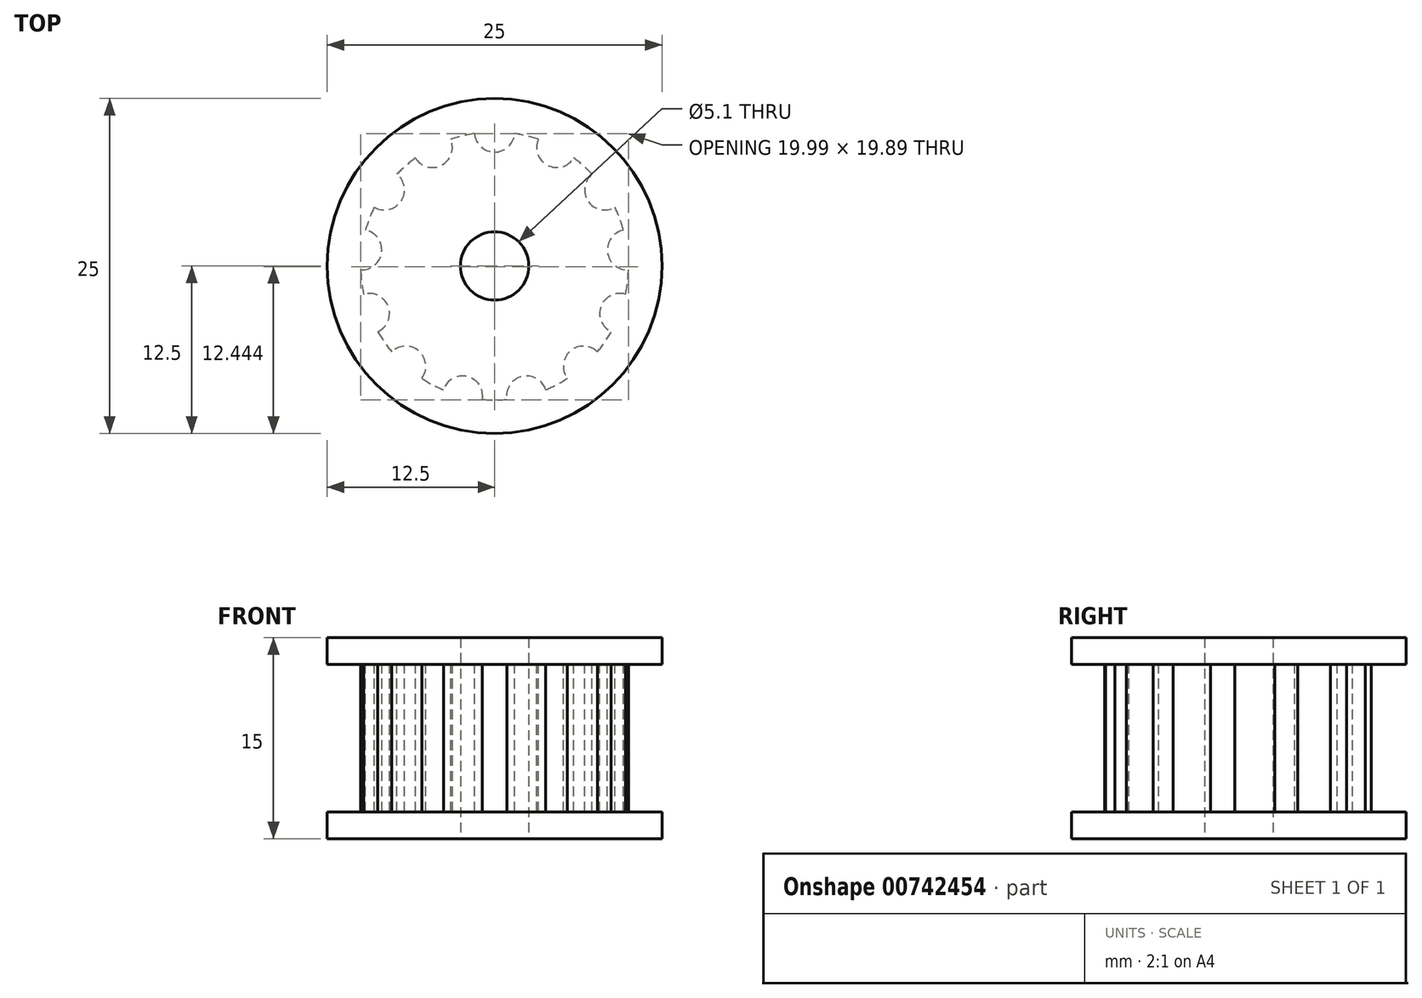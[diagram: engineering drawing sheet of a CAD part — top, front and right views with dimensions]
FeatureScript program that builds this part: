
annotation { "Feature Type Name" : "Feature", "Feature Type Description" : "" }
export const myFeature = defineFeature(function(context is Context, id is Id, definition is map)
    precondition{}
    {
        {
            var Q0;
            Q0=qCreatedBy(makeId("Top.planeOp"),FACE);
            var sketch = newSketch(context, id + "F0", { "sketchPlane" : qUnion([Q0])});
            skCircle(sketch, "E0", {"center": v(0, 0) * mm, "radius": 10 * mm});
            skSolve(sketch);
        }
        {
            var Q0;
            Q0=makeQuery(id+"F0.imprint","IMPRINT",FACE,{"disambiguationData":[TD([[makeQuery(id+"F0.imprint","IMPRINT",EDGE,{"derivedFrom":sQuery(id+"F0.wireOp",EDGE,"E0")}),1.0]])]});
            extrude(context, id + "F1", {"entities" : qUnion([Q0]), "depth" : 11 * mm, "offsetDistance" : 25 * mm});
        }
        {
            var Q0;
            Q0=makeQuery(id+"F1.opExtrude","CAP_FACE",FACE,{"disambiguationData":[OSD([sQuery(id+"F0.wireOp",EDGE,"E0")])],"isStart":false});
            var sketch = newSketch(context, id + "F2", { "sketchPlane" : qUnion([Q0])});
            skLineSegment(sketch, "E1", {"start": v(0, 0) * mm, "end": v(0, 10) * mm, "construction": true});
            skCircle(sketch, "E2", {"center": v(0, 10) * mm, "radius": 1.5 * mm});
            skCircle(sketch, "E3.1.0", {"center": v(-4.65, 8.85) * mm, "radius": 1.5 * mm});
            skCircle(sketch, "E3.2.0", {"center": v(-8.23, 5.68) * mm, "radius": 1.5 * mm});
            skCircle(sketch, "E3.3.0", {"center": v(-9.93, 1.2) * mm, "radius": 1.5 * mm});
            skCircle(sketch, "E3.4.0", {"center": v(-9.35, -3.55) * mm, "radius": 1.5 * mm});
            skCircle(sketch, "E3.5.0", {"center": v(-6.63, -7.49) * mm, "radius": 1.5 * mm});
            skCircle(sketch, "E3.6.0", {"center": v(-2.4, -9.7) * mm, "radius": 1.5 * mm});
            skCircle(sketch, "E3.7.0", {"center": v(2.4, -9.7) * mm, "radius": 1.5 * mm});
            skCircle(sketch, "E3.8.0", {"center": v(6.63, -7.49) * mm, "radius": 1.5 * mm});
            skCircle(sketch, "E3.9.0", {"center": v(9.35, -3.55) * mm, "radius": 1.5 * mm});
            skCircle(sketch, "E3.10.0", {"center": v(9.93, 1.2) * mm, "radius": 1.5 * mm});
            skCircle(sketch, "E3.11.0", {"center": v(8.23, 5.68) * mm, "radius": 1.5 * mm});
            skCircle(sketch, "E3.12.0", {"center": v(4.65, 8.85) * mm, "radius": 1.5 * mm});
            skPoint(sketch, "E3.center", {"position": v(0, 0) * mm});
            skSolve(sketch);
        }
        {
            var Q0;
            Q0 = qSketchRegion(id + "F2", true);
            extrude(context, id + "F3", {"entities" : qUnion([Q0]), "operationType" : NewBodyOperationType.REMOVE, "oppositeDirection" : true, "depth" : 25 * mm, "offsetDistance" : 25 * mm});
        }
        {
            var Q0;
            Q0=makeQuery(id+"F1.opExtrude","CAP_FACE",FACE,{"disambiguationData":[OSD([sQuery(id+"F0.wireOp",EDGE,"E0")])],"isStart":true});
            var sketch = newSketch(context, id + "F4", { "sketchPlane" : qUnion([Q0])});
            skCircle(sketch, "E4", {"center": v(0, 0) * mm, "radius": 12.5 * mm});
            skSolve(sketch);
        }
        {
            var Q0;
            Q0 = qSketchRegion(id + "F4", true);
            extrude(context, id + "F5", {"entities" : qUnion([Q0]), "operationType" : NewBodyOperationType.ADD, "depth" : 2 * mm, "offsetDistance" : 25 * mm});
        }
        {
            var Q0;
            Q0=makeQuery(id+"F1.opExtrude","CAP_FACE",FACE,{"disambiguationData":[OSD([sQuery(id+"F0.wireOp",EDGE,"E0")])],"isStart":false});
            var sketch = newSketch(context, id + "F6", { "sketchPlane" : qUnion([Q0])});
            skCircle(sketch, "E5", {"center": v(0, 0) * mm, "radius": 12.5 * mm});
            skSolve(sketch);
        }
        {
            var Q0;
            Q0 = qSketchRegion(id + "F6", true);
            extrude(context, id + "F7", {"entities" : qUnion([Q0]), "operationType" : NewBodyOperationType.ADD, "depth" : 2 * mm, "offsetDistance" : 25 * mm});
        }
        {
            var Q0;
            Q0=makeQuery(id+"F5.opExtrude","CAP_FACE",FACE,{"disambiguationData":[OSD([sQuery(id+"F4.wireOp",EDGE,"E4")])],"isStart":false});
            var sketch = newSketch(context, id + "F8", { "sketchPlane" : qUnion([Q0])});
            skCircle(sketch, "E6", {"center": v(0, 0) * mm, "radius": 2.55 * mm});
            skSolve(sketch);
        }
        {
            var Q0;
            Q0 = qSketchRegion(id + "F8", true);
            extrude(context, id + "F9", {"entities" : qUnion([Q0]), "operationType" : NewBodyOperationType.REMOVE, "endBound" : BoundingType.THROUGH_ALL, "oppositeDirection" : true, "depth" : 25 * mm, "offsetDistance" : 25 * mm});
        }
    });
